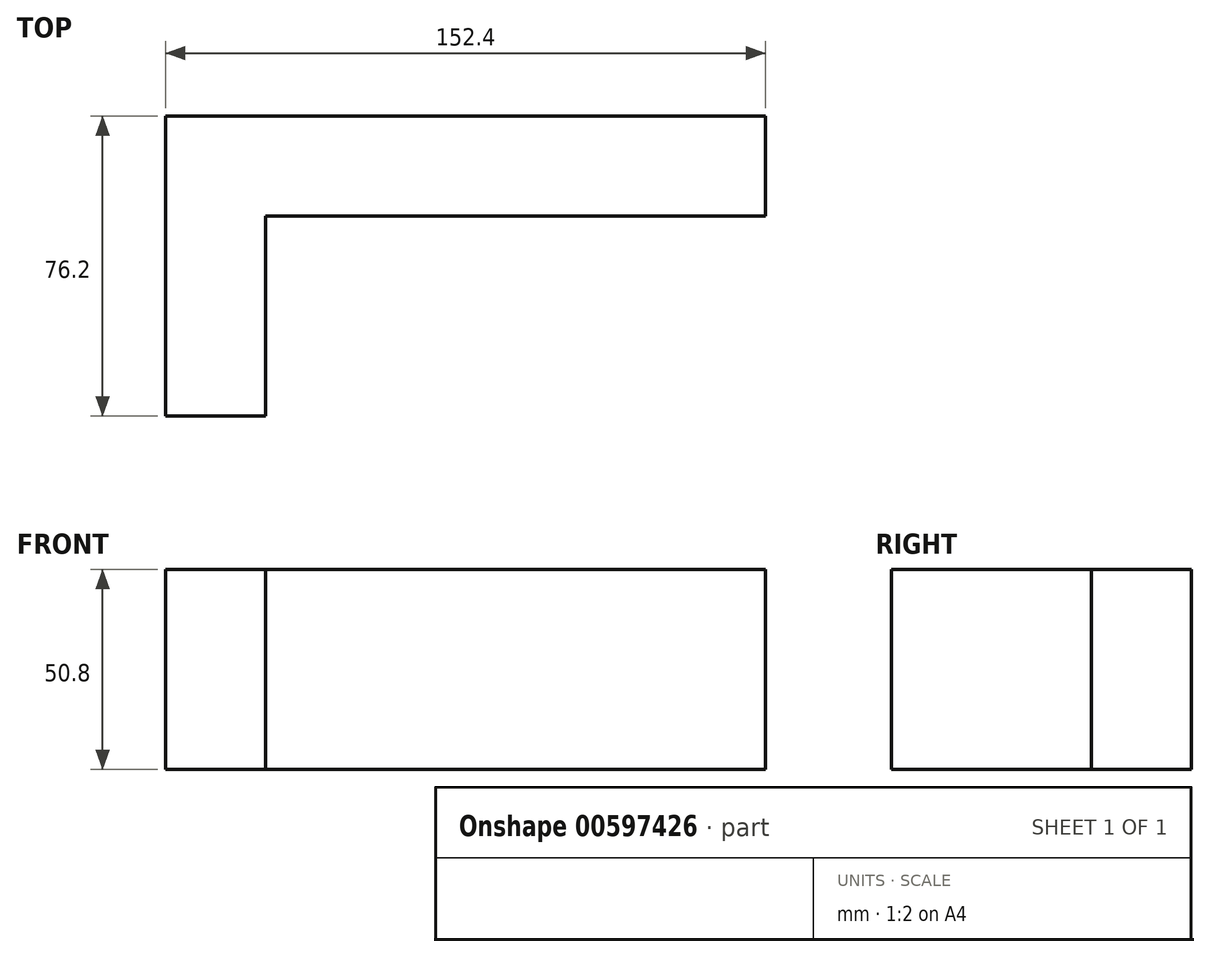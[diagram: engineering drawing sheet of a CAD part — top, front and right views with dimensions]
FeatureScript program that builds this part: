
annotation { "Feature Type Name" : "Feature", "Feature Type Description" : "" }
export const myFeature = defineFeature(function(context is Context, id is Id, definition is map)
    precondition{}
    {
        {
            var Q0;
            Q0=qCreatedBy(makeId("Top.planeOp"),FACE);
            var sketch = newSketch(context, id + "F0", { "sketchPlane" : qUnion([Q0])});
            skLineSegment(sketch, "E0", {"start": v(0, 0) * mm, "end": v(0, 76.2) * mm});
            skLineSegment(sketch, "E1", {"start": v(0, 76.2) * mm, "end": v(152.4, 76.2) * mm});
            skLineSegment(sketch, "E2", {"start": v(152.4, 76.2) * mm, "end": v(152.4, 50.8) * mm});
            skLineSegment(sketch, "E3", {"start": v(152.4, 50.8) * mm, "end": v(25.4, 50.8) * mm});
            skLineSegment(sketch, "E4", {"start": v(25.4, 50.8) * mm, "end": v(25.4, 0) * mm});
            skLineSegment(sketch, "E5", {"start": v(25.4, 0) * mm, "end": v(0, 0) * mm});
            skLineSegment(sketch, "E6", {"start": v(25.4, 50.8) * mm, "end": v(76.24, 50.8) * mm});
            skLineSegment(sketch, "E7", {"start": v(76.24, 50.8) * mm, "end": v(25.4, 25.4) * mm});
            skLineSegment(sketch, "E8", {"start": v(25.4, 25.4) * mm, "end": v(25.4, 50.8) * mm});
            skSolve(sketch);
        }
        {
            var Q0;
            Q0=makeQuery(id+"F0.imprint","IMPRINT",FACE,{"disambiguationData":[TD([[makeQuery(id+"F0.imprint","IMPRINT",EDGE,{"derivedFrom":sQuery(id+"F0.wireOp",EDGE,"E0")}),-1.0]])]});
            var Q1;
            Q1=makeQuery(id+"F0.imprint","IMPRINT",FACE,{"disambiguationData":[TD([[makeQuery(id+"F0.imprint","IMPRINT",EDGE,{"derivedFrom":sQuery(id+"F0.wireOp",EDGE,"E6")}),-1.0]])]});
            extrude(context, id + "F1", {"entities" : qUnion([Q0, Q1]), "oppositeDirection" : true, "depth" : 50.8 * mm, "offsetDistance" : 25.4 * mm});
        }
        {
            var Q0;
            Q0=makeQuery(id+"F1.opExtrude","CAP_FACE",FACE,{"disambiguationData":[OSD([sQuery(id+"F0.wireOp",EDGE,"E0"),sQuery(id+"F0.wireOp",EDGE,"E1"),sQuery(id+"F0.wireOp",EDGE,"E2"),sQuery(id+"F0.wireOp",EDGE,"E3"),sQuery(id+"F0.wireOp",EDGE,"E4"),sQuery(id+"F0.wireOp",EDGE,"E5"),sQuery(id+"F0.wireOp",EDGE,"E7")])],"isStart":true});
            var sketch = newSketch(context, id + "F2", { "sketchPlane" : qUnion([Q0])});
            skLineSegment(sketch, "E9", {"start": v(25.4, 25.4) * mm, "end": v(76.24, 50.8) * mm});
            skLineSegment(sketch, "E10", {"start": v(76.24, 50.8) * mm, "end": v(25.4, 50.8) * mm});
            skLineSegment(sketch, "E11", {"start": v(25.4, 50.8) * mm, "end": v(25.4, 25.4) * mm});
            skSolve(sketch);
        }
        {
            var Q0;
            Q0 = qSketchRegion(id + "F2", true);
            extrude(context, id + "F3", {"entities" : qUnion([Q0]), "operationType" : NewBodyOperationType.REMOVE, "oppositeDirection" : true, "depth" : 25.4 * mm, "offsetDistance" : 25.4 * mm});
        }
    });
